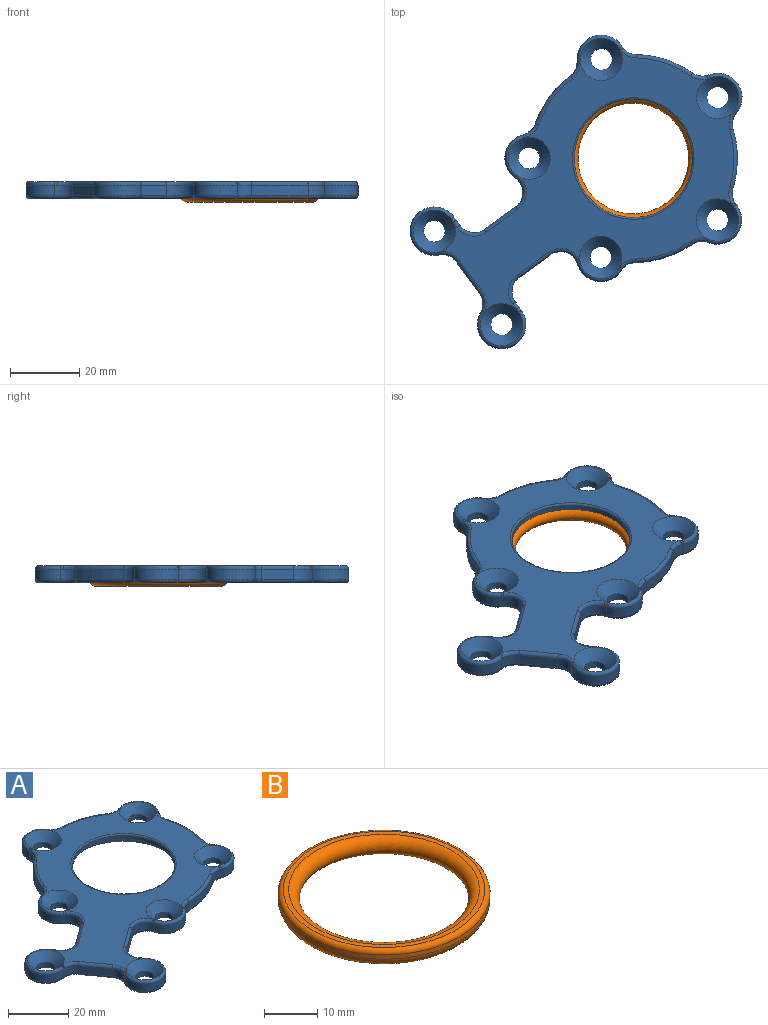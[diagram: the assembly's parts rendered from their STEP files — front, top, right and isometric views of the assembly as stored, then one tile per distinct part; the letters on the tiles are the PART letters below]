
ASSEMBLY  parts=2 mates=1
PART A: 125 faces, bbox 97.4x91.5x5.1 mm
  f0: plane 9.06x6.55mm, normal (0.59,-0.81,0), area 33.5mm2, adj f36,f43,f82,f115
  f1: plane 9.06x6.55mm, normal (-0.59,0.81,0), area 33.5mm2, adj f37,f42,f77,f112
  f2: plane 84.39x75.32mm, normal (0,0,1), area 2029.1mm2, adj f30,f31,f32,f33,f34,f46,f47,f51
  f3: plane 93.65x88.4mm, normal (0,0,-1), area 2321.7mm2, adj f21,f22,f23,f24,f25,f26,f44,f45
  f4: cylinder r=7mm len=12.61mm, axis (0,0,-1), area 48.2mm2, adj f5,f36,f76,f111
  f5: cylinder r=5mm len=4.1mm, axis (0,0,-1), area 14.7mm2, adj f4,f6,f72,f74,f109
  f6: cylinder r=30mm len=16.34mm, axis (0,0,-1), area 52.2mm2, adj f5,f7,f70,f107
  f7: cylinder r=5mm len=4.67mm, axis (0,0,-1), area 14.7mm2, adj f6,f8,f66,f68,f105
  f8: cylinder r=7mm len=11.43mm, axis (0,0,-1), area 55.4mm2, adj f7,f9,f64,f103
  f9: cylinder r=5mm len=4.61mm, axis (0,0,-1), area 14.7mm2, adj f8,f10,f60,f62,f101
  f10: cylinder r=30mm len=17.16mm, axis (0,0,-1), area 52.2mm2, adj f9,f11,f58,f99
  f11: cylinder r=5mm len=4.6mm, axis (0,0,-1), area 14.7mm2, adj f10,f12,f54,f56,f97
  f12: cylinder r=7mm len=11.46mm, axis (0,0,-1), area 55.4mm2, adj f11,f13,f52,f95
  f13: cylinder r=5mm len=4.67mm, axis (0,0,-1), area 14.7mm2, adj f12,f14,f50,f51,f94
  f14: cylinder r=30mm len=16.31mm, axis (0,0,-1), area 52.2mm2, adj f13,f15,f53,f96
  f15: cylinder r=5mm len=4.09mm, axis (0,0,-1), area 14.7mm2, adj f14,f16,f55,f57,f98
  f16: cylinder r=7mm len=12.91mm, axis (0,0,-1), area 55.4mm2, adj f15,f17,f59,f100
  f17: cylinder r=5mm len=4.27mm, axis (0,0,-1), area 14.7mm2, adj f16,f18,f61,f63,f102
  f18: cylinder r=30mm len=13.85mm, axis (0,0,-1), area 52.2mm2, adj f17,f19,f65,f104
  f19: cylinder r=5mm len=3.47mm, axis (0,0,-1), area 14.7mm2, adj f18,f20,f67,f69,f106
  f20: cylinder r=7mm len=12.55mm, axis (0,0,-1), area 48.2mm2, adj f19,f37,f71,f108
  f21: cylinder r=3.1mm len=6.2mm, axis (0,0,-1), area 39mm2, adj f3,f33
  f22: cylinder r=3.1mm len=6.2mm, axis (0,0,-1), area 39mm2, adj f3,f32
  f23: cylinder r=3.1mm len=6.2mm, axis (0,0,-1), area 39mm2, adj f3,f31
  f24: cylinder r=3.1mm len=6.2mm, axis (0,0,-1), area 39mm2, adj f3,f30
  f25: cylinder r=3.1mm len=6.2mm, axis (0,0,-1), area 39mm2, adj f3,f34
  f26: cylinder r=20.05mm len=40.1mm, axis (0,0,-1), area 252mm2, adj f3,f29
  f27: plane 38.1x38.1mm, normal (0,0,-1), area 232.2mm2, adj f28,f29
  f28: cylinder r=17mm len=34mm, axis (0,0,-1), area 160.2mm2, adj f27,f124
  f29: torus R=19.05mm, axis (0,0,-1), area 194.3mm2, adj f26,f27
  f30: cone r=3.1mm half-angle=45deg, axis (0,0,1), area 122.6mm2, adj f2,f24,f62,f64,f66
  f31: cone r=3.1mm half-angle=45deg, axis (0,0,1), area 122.6mm2, adj f2,f23,f50,f52,f54
  f32: cone r=3.1mm half-angle=45deg, axis (0,0,1), area 122.6mm2, adj f2,f22,f57,f59,f61
  f33: cone r=3.1mm half-angle=45deg, axis (0,0,1), area 122.6mm2, adj f2,f21,f69,f71,f73
  f34: cone r=3.1mm half-angle=45deg, axis (0,0,1), area 122.6mm2, adj f2,f25,f74,f76,f78
  f35: plane 9.2x6.64mm, normal (-0.81,-0.59,0), area 34mm2, adj f48,f49,f91,f122
  f36: cylinder r=5mm len=7.73mm, axis (0,0,-1), area 28.7mm2, adj f0,f4,f78,f80,f113
  f37: cylinder r=5mm len=8.18mm, axis (0,0,-1), area 28.7mm2, adj f1,f20,f73,f75,f110
  f38: plane 3.01x2.43mm, normal (0.81,0.59,0), area 9mm2, adj f39,f42,f81,f83,f116
  f39: cylinder r=7mm len=14mm, axis (0,0,1), area 90.1mm2, adj f38,f48,f85,f118
  f40: cylinder r=7mm len=14mm, axis (0,0,1), area 90.1mm2, adj f41,f49,f90,f121
  f41: plane 3.01x2.43mm, normal (0.81,0.59,0), area 9mm2, adj f40,f43,f86,f88,f119
  f42: cylinder r=5mm len=6.98mm, axis (0,0,1), area 23.6mm2, adj f1,f38,f79,f114
  f43: cylinder r=5mm len=6.98mm, axis (0,0,1), area 23.6mm2, adj f0,f41,f84,f117
  f44: cylinder r=3.1mm len=6.2mm, axis (0,0,1), area 39mm2, adj f3,f47
  f45: cylinder r=3.1mm len=6.2mm, axis (0,0,1), area 39mm2, adj f3,f46
  f46: cone r=3.1mm half-angle=45deg, axis (0,0,1), area 122.6mm2, adj f2,f45,f88,f90,f92
  f47: cone r=3.1mm half-angle=45deg, axis (0,0,1), area 122.6mm2, adj f2,f44,f83,f85,f87
  f48: cylinder r=5mm len=5.03mm, axis (0,0,1), area 17.1mm2, adj f35,f39,f87,f89,f120
  f49: cylinder r=5mm len=5.39mm, axis (0,0,1), area 17.1mm2, adj f35,f40,f92,f93,f123
  f50: bspline ~1.49x1.38mm, area 1mm2, adj f13,f31,f51,f52
  f51: torus R=6mm, axis (0,0,1), area 7.2mm2, adj f2,f13,f50,f53
  f52: torus R=6mm, axis (0,0,1), area 25.9mm2, adj f12,f31,f50,f54
  f53: torus R=29mm, axis (0,0,1), area 27mm2, adj f2,f14,f51,f55
  f54: bspline ~1.75x1.74mm, area 1mm2, adj f11,f31,f52,f56
  f55: torus R=6mm, axis (0,0,1), area 7.2mm2, adj f2,f15,f53,f57
  f56: torus R=6mm, axis (0,0,1), area 7.2mm2, adj f2,f11,f54,f58
  f57: bspline ~1.62x1.48mm, area 1mm2, adj f15,f32,f55,f59
  f58: torus R=29mm, axis (0,0,1), area 27mm2, adj f2,f10,f56,f60
  f59: torus R=6mm, axis (0,0,1), area 25.9mm2, adj f16,f32,f57,f61
  f60: torus R=6mm, axis (0,0,1), area 7.2mm2, adj f2,f9,f58,f62
  f61: bspline ~1.36x1.05mm, area 1mm2, adj f17,f32,f59,f63
  f62: bspline ~1.75x1.74mm, area 1mm2, adj f9,f30,f60,f64
  f63: torus R=6mm, axis (0,0,1), area 7.2mm2, adj f2,f17,f61,f65
  f64: torus R=6mm, axis (0,0,1), area 25.9mm2, adj f8,f30,f62,f66
  f65: torus R=29mm, axis (0,0,1), area 27mm2, adj f2,f18,f63,f67
  f66: bspline ~1.49x1.39mm, area 1mm2, adj f7,f30,f64,f68
  f67: torus R=6mm, axis (0,0,1), area 7.2mm2, adj f2,f19,f65,f69
  f68: torus R=6mm, axis (0,0,1), area 7.2mm2, adj f2,f7,f66,f70
  f69: bspline ~1.5x1.25mm, area 1mm2, adj f19,f33,f67,f71
  f70: torus R=29mm, axis (0,0,1), area 27mm2, adj f2,f6,f68,f72
  f71: torus R=6mm, axis (0,0,1), area 22.5mm2, adj f20,f33,f69,f73
  f72: torus R=6mm, axis (0,0,1), area 7.2mm2, adj f2,f5,f70,f74
  f73: bspline ~1.62x1.49mm, area 1mm2, adj f33,f37,f71,f75
  f74: bspline ~1.62x1.48mm, area 1mm2, adj f5,f34,f72,f76
  f75: torus R=6mm, axis (0,0,1), area 15mm2, adj f2,f37,f73,f77
  f76: torus R=6mm, axis (0,0,1), area 22.5mm2, adj f4,f34,f74,f78
  f77: cylinder r=1mm len=9.65mm, axis (-0.81,-0.59,0), area 17.6mm2, adj f1,f2,f75,f79
  f78: bspline ~1.52x1.27mm, area 1mm2, adj f34,f36,f76,f80
  f79: torus R=6mm, axis (0,0,1), area 13.2mm2, adj f2,f42,f77,f81
  f80: torus R=6mm, axis (0,0,1), area 15mm2, adj f2,f36,f78,f82
  f81: cylinder r=1mm len=2.13mm, axis (-0.59,0.81,0), area 3mm2, adj f2,f38,f79,f83
  f82: cylinder r=1mm len=9.65mm, axis (0.81,0.59,0), area 17.6mm2, adj f0,f2,f80,f84
  f83: bspline ~2.14x1.86mm, area 1.7mm2, adj f38,f47,f81,f85
  f84: torus R=6mm, axis (0,0,1), area 13.2mm2, adj f2,f43,f82,f86
  f85: torus R=6mm, axis (0,0,1), area 42mm2, adj f39,f47,f83,f87
  f86: cylinder r=1mm len=2.13mm, axis (-0.59,0.81,0), area 3mm2, adj f2,f41,f84,f88
  f87: bspline ~1.39x1.21mm, area 1mm2, adj f47,f48,f85,f89
  f88: bspline ~2.08x1.95mm, area 1.7mm2, adj f41,f46,f86,f90
  f89: torus R=6mm, axis (0,0,1), area 8.5mm2, adj f2,f48,f87,f91
  f90: torus R=6mm, axis (0,0,1), area 42mm2, adj f40,f46,f88,f92
  f91: cylinder r=1mm len=9.78mm, axis (0.59,-0.81,0), area 17.8mm2, adj f2,f35,f89,f93
  f92: bspline ~1.54x1.49mm, area 1mm2, adj f46,f49,f90,f93
  f93: torus R=6mm, axis (0,0,1), area 8.5mm2, adj f2,f49,f91,f92
  f94: torus R=6mm, axis (0,0,1), area 8.2mm2, adj f3,f13,f95,f96
  f95: torus R=6mm, axis (0,0,1), area 27.5mm2, adj f3,f12,f94,f97
  f96: torus R=29mm, axis (0,0,1), area 27mm2, adj f3,f14,f94,f98
  f97: torus R=6mm, axis (0,0,1), area 8.2mm2, adj f3,f11,f95,f99
  f98: torus R=6mm, axis (0,0,1), area 8.2mm2, adj f3,f15,f96,f100
  f99: torus R=29mm, axis (0,0,1), area 27mm2, adj f3,f10,f97,f101
  f100: torus R=6mm, axis (0,0,1), area 27.5mm2, adj f3,f16,f98,f102
  f101: torus R=6mm, axis (0,0,1), area 8.2mm2, adj f3,f9,f99,f103
  f102: torus R=6mm, axis (0,0,1), area 8.2mm2, adj f3,f17,f100,f104
  f103: torus R=6mm, axis (0,0,1), area 27.5mm2, adj f3,f8,f101,f105
  f104: torus R=29mm, axis (0,0,1), area 27mm2, adj f3,f18,f102,f106
  f105: torus R=6mm, axis (0,0,1), area 8.2mm2, adj f3,f7,f103,f107
  f106: torus R=6mm, axis (0,0,1), area 8.2mm2, adj f3,f19,f104,f108
  f107: torus R=29mm, axis (0,0,1), area 27mm2, adj f3,f6,f105,f109
  f108: torus R=6mm, axis (0,0,1), area 23.9mm2, adj f3,f20,f106,f110
  f109: torus R=6mm, axis (0,0,1), area 8.2mm2, adj f3,f5,f107,f111
  f110: torus R=6mm, axis (0,0,1), area 16.1mm2, adj f3,f37,f108,f112
  f111: torus R=6mm, axis (0,0,1), area 23.9mm2, adj f3,f4,f109,f113
  f112: cylinder r=1mm len=9.65mm, axis (0.81,0.59,0), area 17.6mm2, adj f1,f3,f110,f114
  f113: torus R=6mm, axis (0,0,1), area 16.1mm2, adj f3,f36,f111,f115
  f114: torus R=6mm, axis (0,0,1), area 13.2mm2, adj f3,f42,f112,f116
  f115: cylinder r=1mm len=9.65mm, axis (-0.81,-0.59,0), area 17.6mm2, adj f0,f3,f113,f117
  f116: cylinder r=1mm len=3.02mm, axis (0.59,-0.81,0), area 4.7mm2, adj f3,f38,f114,f118
  f117: torus R=6mm, axis (0,0,1), area 13.2mm2, adj f3,f43,f115,f119
  f118: torus R=6mm, axis (0,0,1), area 44.6mm2, adj f3,f39,f116,f120
  f119: cylinder r=1mm len=3.02mm, axis (0.59,-0.81,0), area 4.7mm2, adj f3,f41,f117,f121
  f120: torus R=6mm, axis (0,0,1), area 9.6mm2, adj f3,f48,f118,f122
  f121: torus R=6mm, axis (0,0,1), area 44.6mm2, adj f3,f40,f119,f123
  f122: cylinder r=1mm len=9.78mm, axis (-0.59,0.81,0), area 17.8mm2, adj f3,f35,f120,f123
  f123: torus R=6mm, axis (0,0,1), area 9.6mm2, adj f3,f49,f121,f122
  f124: torus R=17.5mm, axis (0,0,1), area 84.8mm2, adj f2,f28
PART B: 4 faces, bbox 43.2x43.2x4 mm
  f0: cylinder r=19.95mm len=39.9mm, axis (0,0,1), area 125.3mm2, adj f2,f3
  f1: plane 37.9x37.9mm, normal (0,0,1), area 115.9mm2, adj f2,f3
  f2: torus R=17.95mm, axis (0,0,-1), area 1037.8mm2, adj f0,f1
  f3: torus R=18.95mm, axis (0,0,-1), area 193.3mm2, adj f0,f1
PLACE A at identity
PLACE B at identity
MATE fastened B.f0 <-> A.f6  axis (0,0,1) through (131.64,96.98,32)mm
